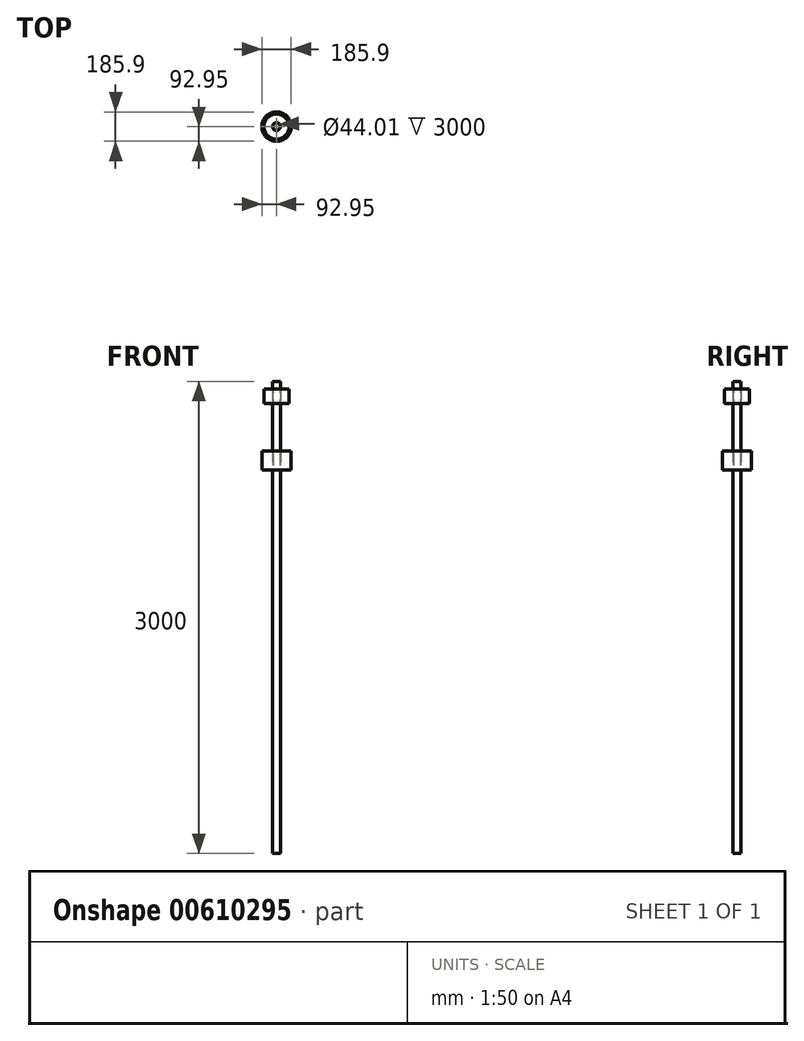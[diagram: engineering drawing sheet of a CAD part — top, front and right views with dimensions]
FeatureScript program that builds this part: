
annotation { "Feature Type Name" : "Feature", "Feature Type Description" : "" }
export const myFeature = defineFeature(function(context is Context, id is Id, definition is map)
    precondition{}
    {
        {
            var Q0;
            Q0=qCreatedBy(makeId("Front.planeOp"),FACE);
            var sketch = newSketch(context, id + "F0", { "sketchPlane" : qUnion([Q0])});
            skLineSegment(sketch, "E0.bottom", {"start": v(-80, 1450.4) * mm, "end": v(80, 1450.4) * mm});
            skLineSegment(sketch, "E0.top", {"start": v(-80, 1358.4) * mm, "end": v(80, 1358.4) * mm});
            skLineSegment(sketch, "E0.left", {"start": v(-80, 1450.4) * mm, "end": v(-80, 1358.4) * mm});
            skLineSegment(sketch, "E0.right", {"start": v(80, 1450.4) * mm, "end": v(80, 1358.4) * mm});
            skLineSegment(sketch, "E1", {"start": v(0, 1358.4) * mm, "end": v(0, 1450.4) * mm, "construction": true});
            skSolve(sketch);
        }
        {
            var Q0;
            Q0=qCreatedBy(makeId("Front.planeOp"),FACE);
            var sketch = newSketch(context, id + "F1", { "sketchPlane" : qUnion([Q0])});
            skLineSegment(sketch, "E2.bottom", {"start": v(-93, 1058.4) * mm, "end": v(93, 1058.4) * mm});
            skLineSegment(sketch, "E2.top", {"start": v(-93, 938.4) * mm, "end": v(93, 938.4) * mm});
            skLineSegment(sketch, "E2.left", {"start": v(-93, 1058.4) * mm, "end": v(-93, 938.4) * mm});
            skLineSegment(sketch, "E2.right", {"start": v(93, 1058.4) * mm, "end": v(93, 938.4) * mm});
            skLineSegment(sketch, "E3", {"start": v(0, 1358.4) * mm, "end": v(0, 1058.4) * mm, "construction": true});
            skSolve(sketch);
        }
        {
            var Q0;
            Q0=qCreatedBy(makeId("Top.planeOp"),FACE);
            var sketch = newSketch(context, id + "F2", { "sketchPlane" : qUnion([Q0])});
            skCircle(sketch, "E4", {"center": v(0, 0) * mm, "radius": 25 * mm});
            skSolve(sketch);
        }
        {
            var Q0;
            Q0=makeQuery(id+"F2.imprint","IMPRINT",FACE,{"disambiguationData":[TD([[makeQuery(id+"F2.imprint","IMPRINT",EDGE,{"derivedFrom":sQuery(id+"F2.wireOp",EDGE,"E4")}),1.0]])]});
            extrude(context, id + "F3", {"entities" : qUnion([Q0]), "endBound" : BoundingType.SYMMETRIC, "depth" : 3000 * mm, "offsetDistance" : 25 * mm});
        }
        {
            var Q0;
            Q0=makeQuery(id+"F3.opExtrude","CAP_FACE",FACE,{"disambiguationData":[OSD([sQuery(id+"F2.wireOp",EDGE,"E4")])],"isStart":false});
            var Q1;
            Q1=makeQuery(id+"F3.opExtrude","CAP_FACE",FACE,{"disambiguationData":[OSD([sQuery(id+"F2.wireOp",EDGE,"E4")])],"isStart":true});
            shell(context, id + "F4", {"entities" : qUnion([Q0, Q1]), "thickness" : 3 * mm});
        }
        {
            var Q0;
            Q0=qCreatedBy(makeId("Top.planeOp"),FACE);
            cPlane(context, id + "F5", {"entities" : qUnion([Q0]), "cplaneType" : CPlaneType.OFFSET, "offset" : 937.5 * mm, "width" : 150 * mm, "height" : 150 * mm});
        }
        {
            var Q0;
            Q0=qCreatedBy(id+"F5.planeOp",FACE);
            var sketch = newSketch(context, id + "F6", { "sketchPlane" : qUnion([Q0])});
            skCircle(sketch, "E5", {"center": v(0, 0) * mm, "radius": 92.95 * mm});
            skSolve(sketch);
        }
        {
            var Q0;
            Q0=makeQuery(id+"F6.imprint","IMPRINT",FACE,{"disambiguationData":[TD([[makeQuery(id+"F6.imprint","IMPRINT",EDGE,{"derivedFrom":sQuery(id+"F6.wireOp",EDGE,"E5")}),1.0]])]});
            extrude(context, id + "F7", {"entities" : qUnion([Q0]), "depth" : 120.5 * mm, "offsetDistance" : 25 * mm});
        }
        {
            var Q0;
            Q0=qCreatedBy(makeId("Top.planeOp"),FACE);
            cPlane(context, id + "F8", {"entities" : qUnion([Q0]), "cplaneType" : CPlaneType.OFFSET, "offset" : 1358.2 * mm, "width" : 150 * mm, "height" : 150 * mm});
        }
        {
            var Q0;
            Q0=qCreatedBy(id+"F8.planeOp",FACE);
            var sketch = newSketch(context, id + "F9", { "sketchPlane" : qUnion([Q0])});
            skCircle(sketch, "E6", {"center": v(0, 0) * mm, "radius": 80 * mm});
            skSolve(sketch);
        }
        {
            var Q0;
            Q0=makeQuery(id+"F9.imprint","IMPRINT",FACE,{"disambiguationData":[TD([[makeQuery(id+"F9.imprint","IMPRINT",EDGE,{"derivedFrom":sQuery(id+"F9.wireOp",EDGE,"E6")}),1.0]])]});
            extrude(context, id + "F10", {"entities" : qUnion([Q0]), "depth" : 92 * mm, "offsetDistance" : 25 * mm});
        }
    });
